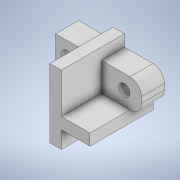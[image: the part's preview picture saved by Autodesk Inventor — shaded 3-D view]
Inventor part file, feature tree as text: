
AUTODESK INVENTOR PART (.ipt)
format: ipt  version: 2021 (Build 250183000, 183)  size: 142,848 bytes
history: native  units: mm
features: sketch x4, extrude x3, hole x1, fillet x1
ambient origin geometry x8: Origin, YZ Plane, XZ Plane, XY Plane, X Axis, Y Axis, Z Axis, Center Point
bodies: Solid1 (feature_tree)
feature tree (9):
  extrude  "Extrusion1"  Depth=5.0mm
  hole  "Hole1"  [1 undecoded]
  extrude  "Extrusion2"  Depth=2.0mm
  fillet  "Fillet1"  Radius=10.0mm
  extrude  "Extrusion3"  Depth=6.0mm
  sketch  "Sketch1"  dims[d0=15.0mm d1=5.0mm]
  sketch  "Sketch2"  dims[d2=4.0mm d3=0.0mm d4=2.5mm]
  sketch  "Sketch3"  dims[d5=2.5mm d6=2.0mm d7=10.0mm]
  sketch  "Sketch4"  dims[d8=2.0mm d9=6.0mm d10=4.0mm d11=2.0mm d12=90.0deg d13=4.0mm d14=20.594885mm d15=6.0mm d16=2.0mm d17=12.0mm d18=2.0mm d19=11.0mm d20=0.0mm d21=2.0mm d22=2.0mm d23=0.0mm]
note: 1 required parameter value undecoded (feature->parameter linkage not recoverable at this tier; creation-order binding heuristic only, values carry confidence <= 0.55)
